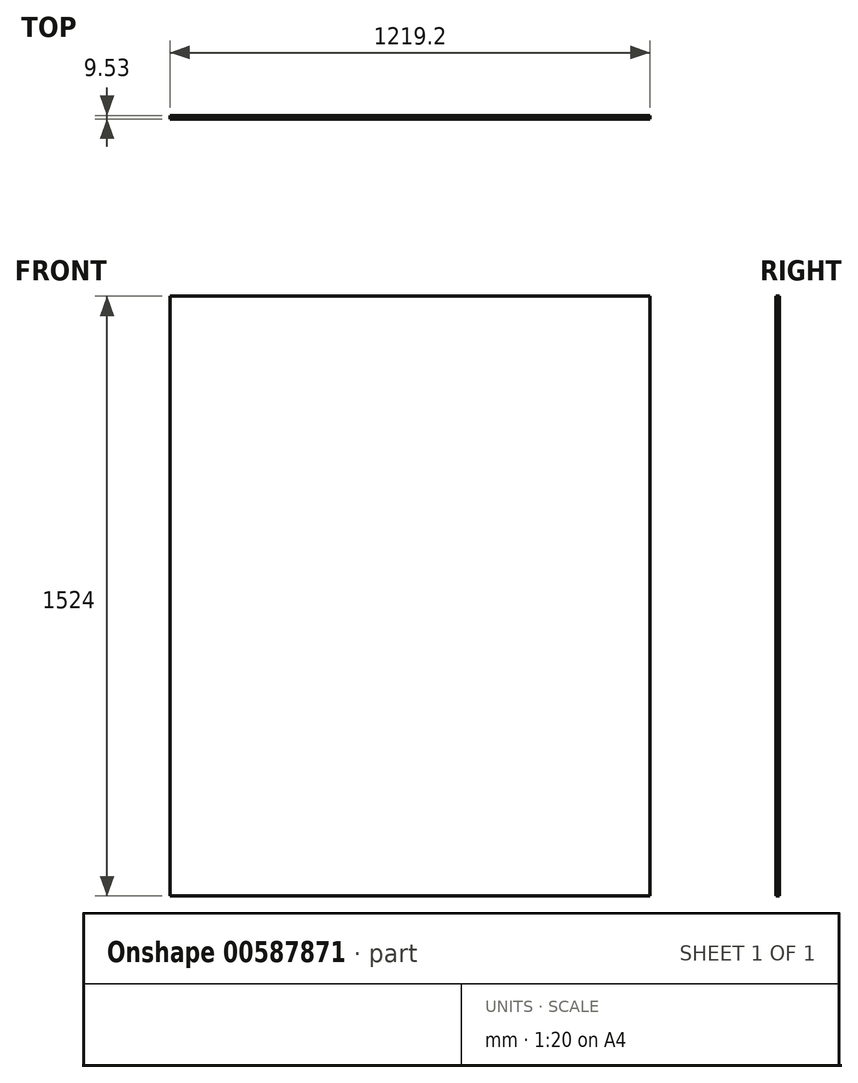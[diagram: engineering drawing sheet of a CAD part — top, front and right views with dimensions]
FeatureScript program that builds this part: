
annotation { "Feature Type Name" : "Feature", "Feature Type Description" : "" }
export const myFeature = defineFeature(function(context is Context, id is Id, definition is map)
    precondition{}
    {
        {
            var Q0;
            Q0=qCreatedBy(makeId("Front.planeOp"),FACE);
            var sketch = newSketch(context, id + "F0", { "sketchPlane" : qUnion([Q0])});
            skLineSegment(sketch, "E0.bottom", {"start": v(609.6, -762) * mm, "end": v(-609.6, -762) * mm});
            skLineSegment(sketch, "E0.top", {"start": v(609.6, 762) * mm, "end": v(-609.6, 762) * mm});
            skLineSegment(sketch, "E0.left", {"start": v(609.6, -762) * mm, "end": v(609.6, 762) * mm});
            skLineSegment(sketch, "E0.right", {"start": v(-609.6, -762) * mm, "end": v(-609.6, 762) * mm});
            skPoint(sketch, "E0.middle", {"position": v(0, 0) * mm});
            skSolve(sketch);
        }
        {
            var Q0;
            Q0 = qSketchRegion(id + "F0", true);
            extrude(context, id + "F1", {"entities" : qUnion([Q0]), "oppositeDirection" : true, "depth" : 9.52 * mm, "offsetDistance" : 25.4 * mm});
        }
    });
